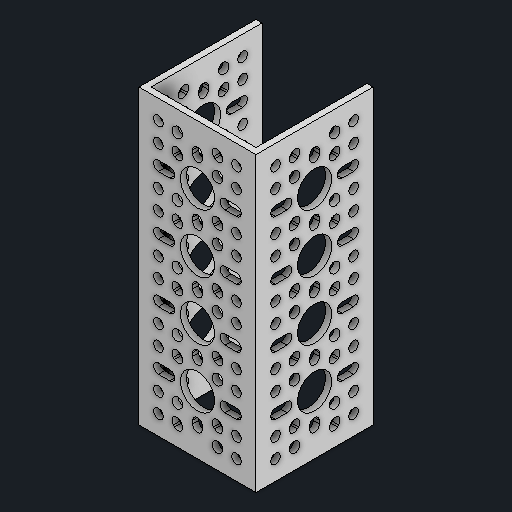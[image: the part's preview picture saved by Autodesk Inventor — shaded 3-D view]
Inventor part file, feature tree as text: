
AUTODESK INVENTOR PART (.ipt)
format: ipt  version: 2024 (Build 280153000, 153)  size: 612,352 bytes
history: native  units: in
note: dims shown in document units (in); Inventor stores cm internally (conversion verified against a paired STEP export)
features: mirror x1
ambient origin geometry x8: Origin, YZ Plane, XZ Plane, XY Plane, X Axis, Y Axis, Z Axis, Center Point
bodies: Solid1 (feature_tree)
feature tree (1):
  mirror  "Mirror5"
